# Revit family: Satellite 3 Chandelier
name_source: partatom
category: Lighting Fixtures
revit_build: Autodesk Revit 2017 (Build: 20190508_0315(x64)
units: mm (PartAtom-declared; Revit-internal decimal feet)

## family parameters
Cut with Voids When Loaded = No
Host = Face
Light Source = Yes
Part Type = Normal
Room Calculation Point = No
Round Connector Dimension = Use Diameter
Shared = No

## types (1)
- Satellite 3 Chandelier
    Canopy Width = 5"
    Color Filter = 16777215
    Cost = 399 $
    Default Elevation = 0"
    Description = The Satellite Chandelier places pared down and honest components in a striking orbital arrangement. Part of a lighting family that channels the spirit of early 20th century industrial fixtures, the Satellite 3 Chandelier lends itself to a vintage look with exposed filament bulbs, or a brilliant modern aesthetic with silver-tipped bulbs. Assembled in our Portland, Ore. factory using ethically-sourced domestic and global components. A Schoolhouse Original.
    Dimming Lamp Color Temperature Shift = <None>
    Height = 15 1/4"
    Light Source Symbol Size = 2 1/4"
    Max Wattage = 60 W
    Primary Finishes = Natural Brass, True Black
    Product Material = Schoolhouse_Brass
    URL = https://www.schoolhouse.com
    Voltage = 120 /220V
    Width = 6"

## geometry (parser evidence)
native form markers: Sweep x3
no freeform markers — native parametric forms only
